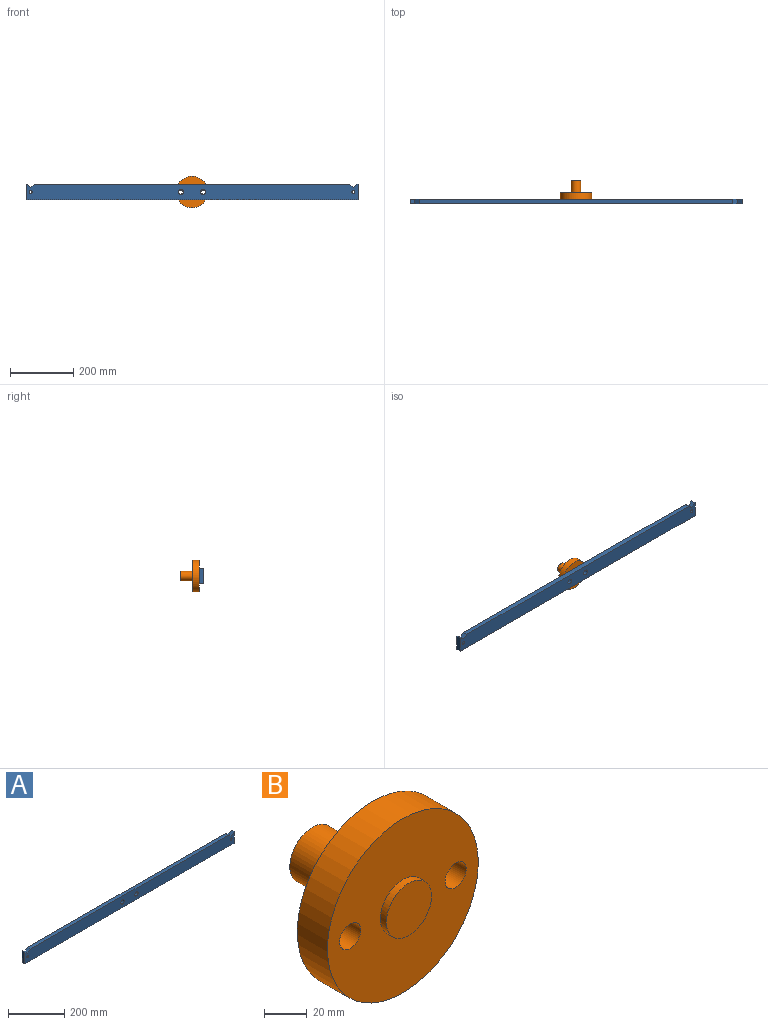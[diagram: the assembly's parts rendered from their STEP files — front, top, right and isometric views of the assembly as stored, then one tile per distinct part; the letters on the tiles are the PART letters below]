
ASSEMBLY  parts=2 mates=1
PART A: 16 faces, bbox 1050x15x50 mm
  f0: plane 50x15mm, normal (1,0,0), area 750mm2, adj f1,f7,f8,f9
  f1: plane 15x14.8mm, normal (-0.56,0,0.83), area 267.9mm2, adj f0,f2,f8,f9
  f2: plane 15x14.8mm, normal (0.56,0,0.83), area 267.9mm2, adj f1,f3,f8,f9
  f3: plane 990.8x15mm, normal (0,0,1), area 14862mm2, adj f2,f4,f8,f9
  f4: plane 15x14.8mm, normal (-0.56,0,0.83), area 267.9mm2, adj f3,f5,f8,f9
  f5: plane 15x14.8mm, normal (0.56,0,0.83), area 267.9mm2, adj f4,f6,f8,f9
  f6: plane 50x15mm, normal (-1,0,0), area 750mm2, adj f5,f7,f8,f9
  f7: plane 1050x15mm, normal (0,0,-1), area 15750mm2, adj f0,f6,f8,f9
  f8: plane 1050x50mm, normal (0,-1,0), area 51593mm2, adj f0,f1,f2,f3,f4,f5,f6,f7
  f9: plane 1050x50mm, normal (0,1,0), area 50886.1mm2, adj f0,f1,f2,f3,f4,f5,f6,f7
  f10: cylinder r=15mm len=30mm, axis (0,1,0), area 471.2mm2, adj f9,f11
  f11: plane 30x30mm, normal (0,1,0), area 706.9mm2, adj f10
  f12: cylinder r=8.5mm len=17mm, axis (0,1,0), area 801.1mm2, adj f8,f9
  f13: cylinder r=8.5mm len=17mm, axis (0,1,0), area 801.1mm2, adj f8,f9
  f14: cylinder r=5mm len=15mm, axis (0,1,0), area 471.2mm2, adj f8,f9
  f15: cylinder r=5mm len=15mm, axis (0,1,0), area 471.2mm2, adj f8,f9
PART B: 11 faces, bbox 100x64x100 mm
  f0: plane 30x30mm, normal (0,-1,0), area 706.9mm2, adj f8
  f1: plane 22x22mm, normal (0,1,0), area 380.1mm2, adj f2
  f2: cylinder r=11mm len=40mm, axis (0,1,0), area 2764.6mm2, adj f1,f3
  f3: plane 30x30mm, normal (0,1,0), area 326.7mm2, adj f2,f4
  f4: cylinder r=15mm len=40mm, axis (0,1,0), area 3769.9mm2, adj f3,f5
  f5: plane 100x100mm, normal (0,1,0), area 6839.2mm2, adj f4,f6,f9,f10
  f6: cylinder r=50mm len=100mm, axis (0,1,0), area 6283.2mm2, adj f5,f7
  f7: plane 100x100mm, normal (0,-1,0), area 6839.2mm2, adj f6,f8,f9,f10
  f8: cylinder r=15mm len=30mm, axis (0,1,0), area 377mm2, adj f0,f7
  f9: cylinder r=7mm len=20mm, axis (0,-1,0), area 879.6mm2, adj f5,f7
  f10: cylinder r=7mm len=20mm, axis (0,-1,0), area 879.6mm2, adj f5,f7
PLACE A t=(370.39,388.3,4.07)mm
PLACE B t=(370.39,419.66,81.23)mm
MATE pin_slot A.f10 <-> B.f2  axis (0,1,0) through (370.39,388.3,81.23)mm
